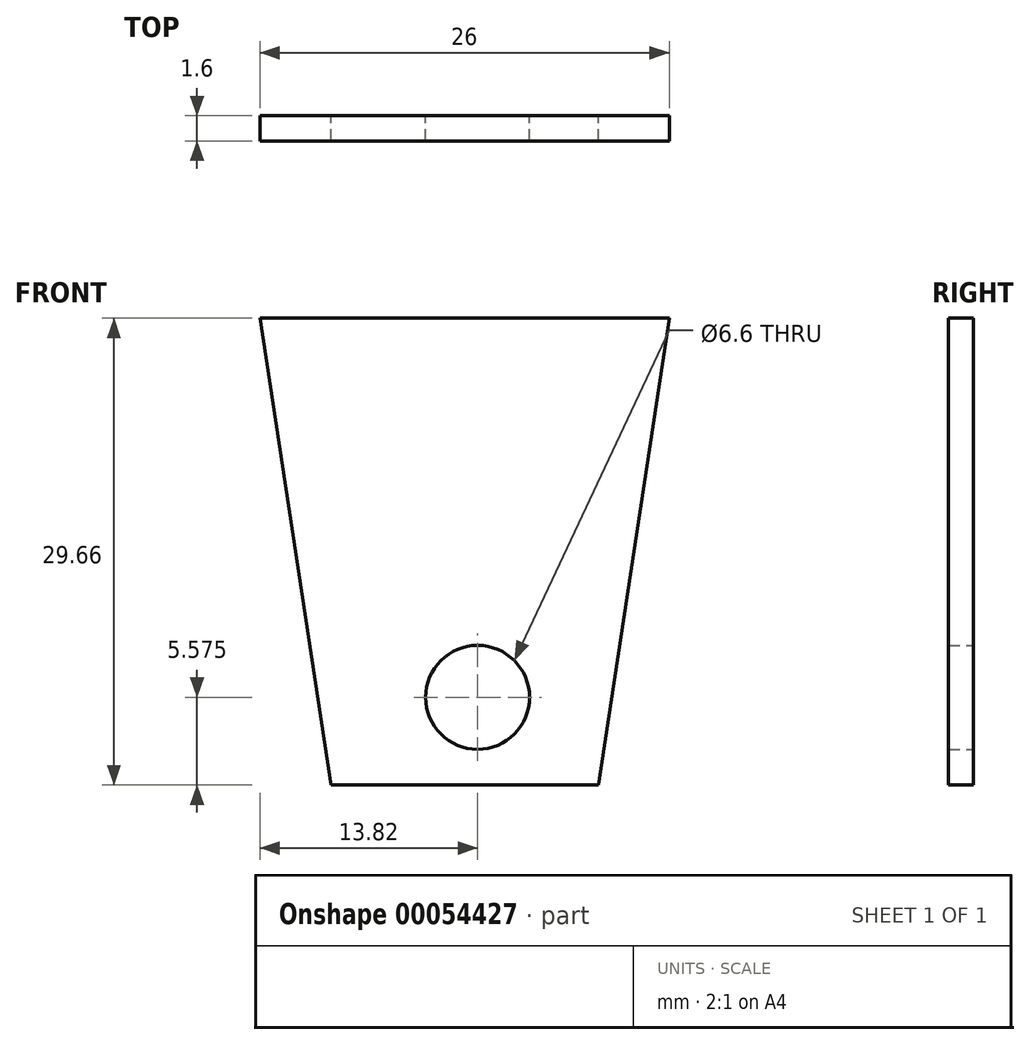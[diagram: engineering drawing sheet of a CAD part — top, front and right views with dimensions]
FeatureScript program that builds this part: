
annotation { "Feature Type Name" : "Feature", "Feature Type Description" : "" }
export const myFeature = defineFeature(function(context is Context, id is Id, definition is map)
    precondition{}
    {
        {
            var Q0;
            Q0=qCreatedBy(makeId("Front.planeOp"),FACE);
            var sketch = newSketch(context, id + "F0", { "sketchPlane" : qUnion([Q0])});
            skLineSegment(sketch, "E0", {"start": v(-13.82, 50.6) * mm, "end": v(12.18, 50.6) * mm});
            skLineSegment(sketch, "E1", {"start": v(-13.82, 50.6) * mm, "end": v(-9.32, 20.94) * mm});
            skLineSegment(sketch, "E2", {"start": v(-9.32, 20.94) * mm, "end": v(7.68, 20.94) * mm});
            skLineSegment(sketch, "E3", {"start": v(7.68, 20.94) * mm, "end": v(12.18, 50.6) * mm});
            skCircle(sketch, "E4", {"center": v(0, 26.51) * mm, "radius": 3.3 * mm});
            skSolve(sketch);
        }
        {
            var Q0;
            Q0=makeQuery(id+"F0.imprint","IMPRINT",FACE,{"disambiguationData":[TD([[makeQuery(id+"F0.imprint","IMPRINT",EDGE,{"derivedFrom":sQuery(id+"F0.wireOp",EDGE,"E0")}),-1.0]])]});
            extrude(context, id + "F1", {"entities" : qUnion([Q0]), "depth" : 1.6 * mm});
        }
    });
